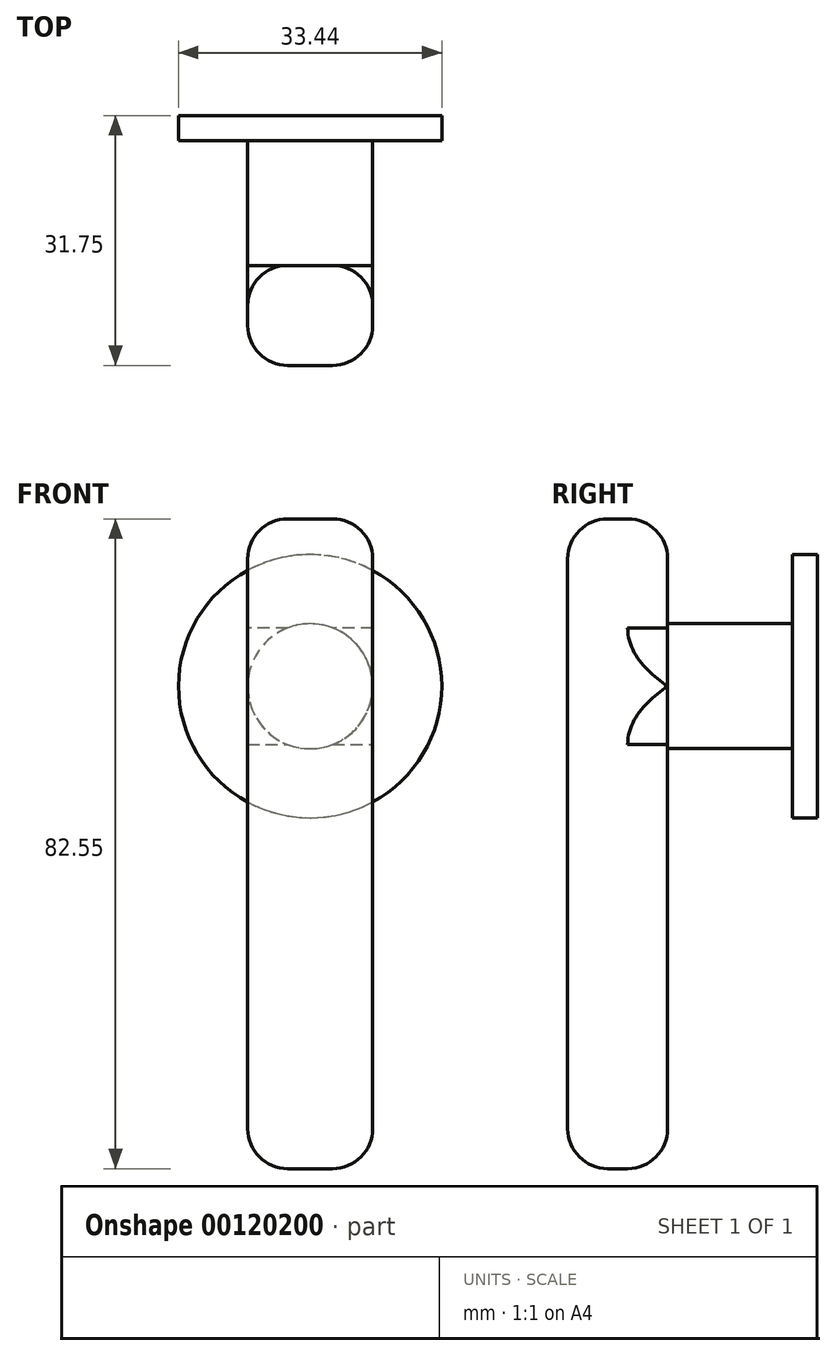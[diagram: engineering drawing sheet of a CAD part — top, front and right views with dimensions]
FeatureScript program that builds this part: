
annotation { "Feature Type Name" : "Feature", "Feature Type Description" : "" }
export const myFeature = defineFeature(function(context is Context, id is Id, definition is map)
    precondition{}
    {
        {
            var Q0;
            Q0=qCreatedBy(makeId("Right.planeOp"),FACE);
            var sketch = newSketch(context, id + "F0", { "sketchPlane" : qUnion([Q0])});
            skLineSegment(sketch, "E0.bottom", {"start": v(0, 0) * mm, "end": v(-15.88, 0) * mm});
            skLineSegment(sketch, "E0.top", {"start": v(0, 15.88) * mm, "end": v(-15.88, 15.88) * mm});
            skLineSegment(sketch, "E0.left", {"start": v(0, 0) * mm, "end": v(0, 15.88) * mm});
            skLineSegment(sketch, "E0.right", {"start": v(-15.88, 0) * mm, "end": v(-15.88, 15.88) * mm});
            skLineSegment(sketch, "E1.bottom", {"start": v(-15.88, 29.2) * mm, "end": v(-28.58, 29.2) * mm});
            skLineSegment(sketch, "E1.top", {"start": v(-15.88, -53.35) * mm, "end": v(-28.57, -53.35) * mm});
            skLineSegment(sketch, "E1.left", {"start": v(-15.88, 29.2) * mm, "end": v(-15.88, -53.35) * mm});
            skLineSegment(sketch, "E1.right", {"start": v(-28.58, 29.2) * mm, "end": v(-28.57, -53.35) * mm});
            skSolve(sketch);
        }
        {
            var Q0;
            Q0 = qSketchRegion(id + "F0", true);
            extrude(context, id + "F1", {"entities" : qUnion([Q0]), "endBound" : BoundingType.SYMMETRIC, "depth" : 15.88 * mm});
        }
        {
            var Q0;
            Q0=makeQuery(id+"F1.opExtrude","CAP_EDGE",EDGE,{"disambiguationData":[OSD([sQuery(id+"F0.wireOp",EDGE,"E0.top")])],"isStart":false});
            var Q1;
            Q1=makeQuery(id+"F1.opExtrude","CAP_EDGE",EDGE,{"disambiguationData":[OSD([sQuery(id+"F0.wireOp",EDGE,"E0.bottom")])],"isStart":false});
            var Q2;
            Q2=makeQuery(id+"F1.opExtrude","CAP_EDGE",EDGE,{"disambiguationData":[OSD([sQuery(id+"F0.wireOp",EDGE,"E0.top")])],"isStart":true});
            var Q3;
            Q3=makeQuery(id+"F1.opExtrude","CAP_EDGE",EDGE,{"disambiguationData":[OSD([sQuery(id+"F0.wireOp",EDGE,"E0.bottom")])],"isStart":true});
            fillet(context, id + "F2", {"entities" : qUnion([Q0, Q1, Q2, Q3]), "radius" : 7.94 * mm, "tangentPropagation" : true, "allowEdgeOverflow" : false});
        }
        {
            var Q0;
            Q0=makeQuery(id+"F1.opExtrude","CAP_EDGE",EDGE,{"disambiguationData":[OSD([sQuery(id+"F0.wireOp",EDGE,"E1.right")])],"isStart":true});
            var Q1;
            Q1=makeQuery(id+"F1.opExtrude","CAP_EDGE",EDGE,{"disambiguationData":[OSD([sQuery(id+"F0.wireOp",EDGE,"E1.right")])],"isStart":false});
            var Q2;
            Q2=makeQuery(id+"F1.opExtrude","SWEPT_EDGE",EDGE,{"disambiguationData":[OSD([sQuery(id+"F0.wireOp",EDGE,"E1.top"),sQuery(id+"F0.wireOp",EDGE,"E1.right")])]});
            var Q3;
            Q3=makeQuery(id+"F1.opExtrude","SWEPT_EDGE",EDGE,{"disambiguationData":[OSD([sQuery(id+"F0.wireOp",EDGE,"E1.bottom"),sQuery(id+"F0.wireOp",EDGE,"E1.right")])]});
            var Q4;
            Q4=makeQuery(id+"F1.opExtrude","SWEPT_EDGE",EDGE,{"disambiguationData":[OSD([sQuery(id+"F0.wireOp",EDGE,"E1.top"),sQuery(id+"F0.wireOp",EDGE,"E1.left")])]});
            var Q5;
            Q5=makeQuery(id+"F1.opExtrude","CAP_EDGE",EDGE,{"disambiguationData":[OSD([sQuery(id+"F0.wireOp",EDGE,"E1.top")])],"isStart":false});
            var Q6;
            Q6=makeQuery(id+"F1.opExtrude","CAP_EDGE",EDGE,{"disambiguationData":[OSD([sQuery(id+"F0.wireOp",EDGE,"E1.top")])],"isStart":true});
            var Q7;
            {var subQ0=sQuery(id+"F0.wireOp",EDGE,"E1.left");Q7=makeQuery(id+"F1.opExtrude","CAP_EDGE",EDGE,{"disambiguationData":[OSD([subQ0]),TDD([makeQuery(id+"F0.imprint","IMPRINT",EDGE,{"disambiguationData":[TD([[makeQuery(id+"F0.imprint","INTERSECT",VERTEX,{"derivedFrom":[sQuery(id+"F0.wireOp",EDGE,"E0.bottom"),subQ0]}),-1.0]])],"derivedFrom":subQ0})])],"isStart":true});}
            var Q8;
            {var subQ0=sQuery(id+"F0.wireOp",EDGE,"E1.left");Q8=makeQuery(id+"F1.opExtrude","CAP_EDGE",EDGE,{"disambiguationData":[OSD([subQ0]),TDD([makeQuery(id+"F0.imprint","IMPRINT",EDGE,{"disambiguationData":[TD([[makeQuery(id+"F0.imprint","INTERSECT",VERTEX,{"derivedFrom":[sQuery(id+"F0.wireOp",EDGE,"E0.bottom"),subQ0]}),-1.0]])],"derivedFrom":subQ0})])],"isStart":false});}
            var Q9;
            Q9=makeQuery(id+"F1.opExtrude","SWEPT_EDGE",EDGE,{"disambiguationData":[OSD([sQuery(id+"F0.wireOp",EDGE,"E1.bottom"),sQuery(id+"F0.wireOp",EDGE,"E1.left")])]});
            var Q10;
            Q10=makeQuery(id+"F1.opExtrude","CAP_EDGE",EDGE,{"disambiguationData":[OSD([sQuery(id+"F0.wireOp",EDGE,"E1.bottom")])],"isStart":false});
            var Q11;
            Q11=makeQuery(id+"F1.opExtrude","CAP_EDGE",EDGE,{"disambiguationData":[OSD([sQuery(id+"F0.wireOp",EDGE,"E1.bottom")])],"isStart":true});
            fillet(context, id + "F3", {"entities" : qUnion([Q0, Q1, Q2, Q3, Q4, Q5, Q6, Q7, Q8, Q9, Q10, Q11]), "radius" : 5.08 * mm, "tangentPropagation" : true, "allowEdgeOverflow" : false});
        }
        {
            var Q0;
            Q0=makeQuery(id+"F1.opExtrude","SWEPT_FACE",FACE,{"disambiguationData":[OSD([sQuery(id+"F0.wireOp",EDGE,"E0.left")])]});
            var sketch = newSketch(context, id + "F4", { "sketchPlane" : qUnion([Q0])});
            skCircle(sketch, "E2", {"center": v(0, 7.94) * mm, "radius": 16.72 * mm});
            skSolve(sketch);
        }
        {
            var Q0;
            Q0 = qSketchRegion(id + "F4", true);
            extrude(context, id + "F5", {"entities" : qUnion([Q0]), "operationType" : NewBodyOperationType.ADD, "depth" : 3.17 * mm});
        }
    });
